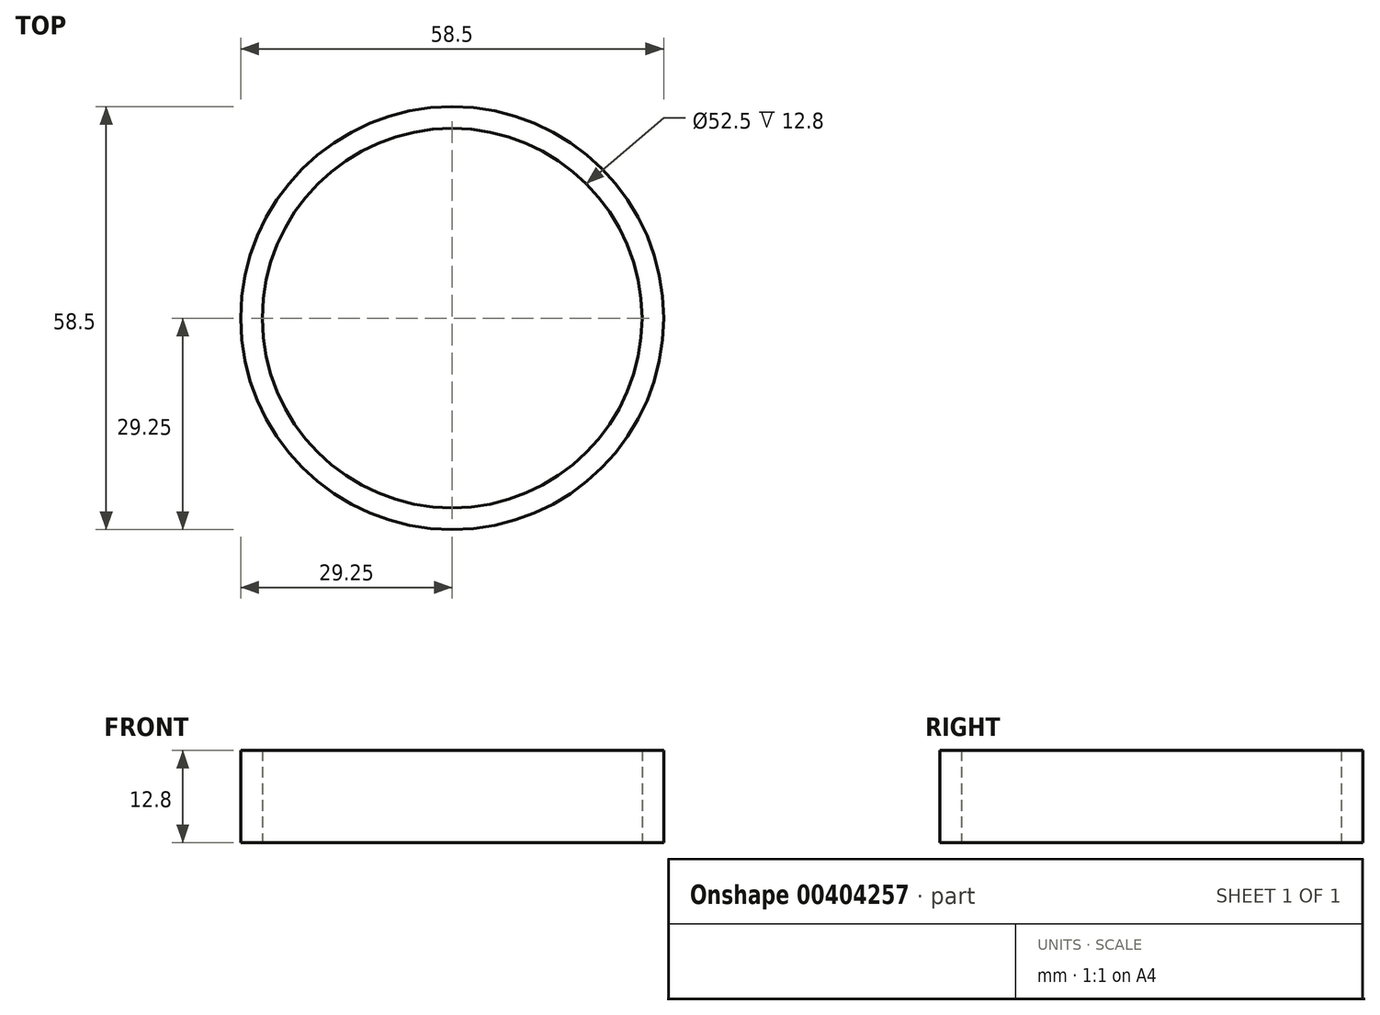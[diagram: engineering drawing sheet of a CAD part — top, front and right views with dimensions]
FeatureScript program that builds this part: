
annotation { "Feature Type Name" : "Feature", "Feature Type Description" : "" }
export const myFeature = defineFeature(function(context is Context, id is Id, definition is map)
    precondition{}
    {
        {
            var Q0;
            Q0=qCreatedBy(makeId("Top.planeOp"),FACE);
            var sketch = newSketch(context, id + "F0", { "sketchPlane" : qUnion([Q0])});
            skCircle(sketch, "E0", {"center": v(0, 0) * mm, "radius": 26.25 * mm});
            skCircle(sketch, "E1", {"center": v(0, 0) * mm, "radius": 29.25 * mm});
            skSolve(sketch);
        }
        {
            var Q0;
            Q0=makeQuery(id+"F0.imprint","IMPRINT",FACE,{"disambiguationData":[TD([[makeQuery(id+"F0.imprint","IMPRINT",EDGE,{"derivedFrom":sQuery(id+"F0.wireOp",EDGE,"E0")}),-1.0]])]});
            extrude(context, id + "F1", {"entities" : qUnion([Q0]), "depth" : 12.8 * mm});
        }
    });
